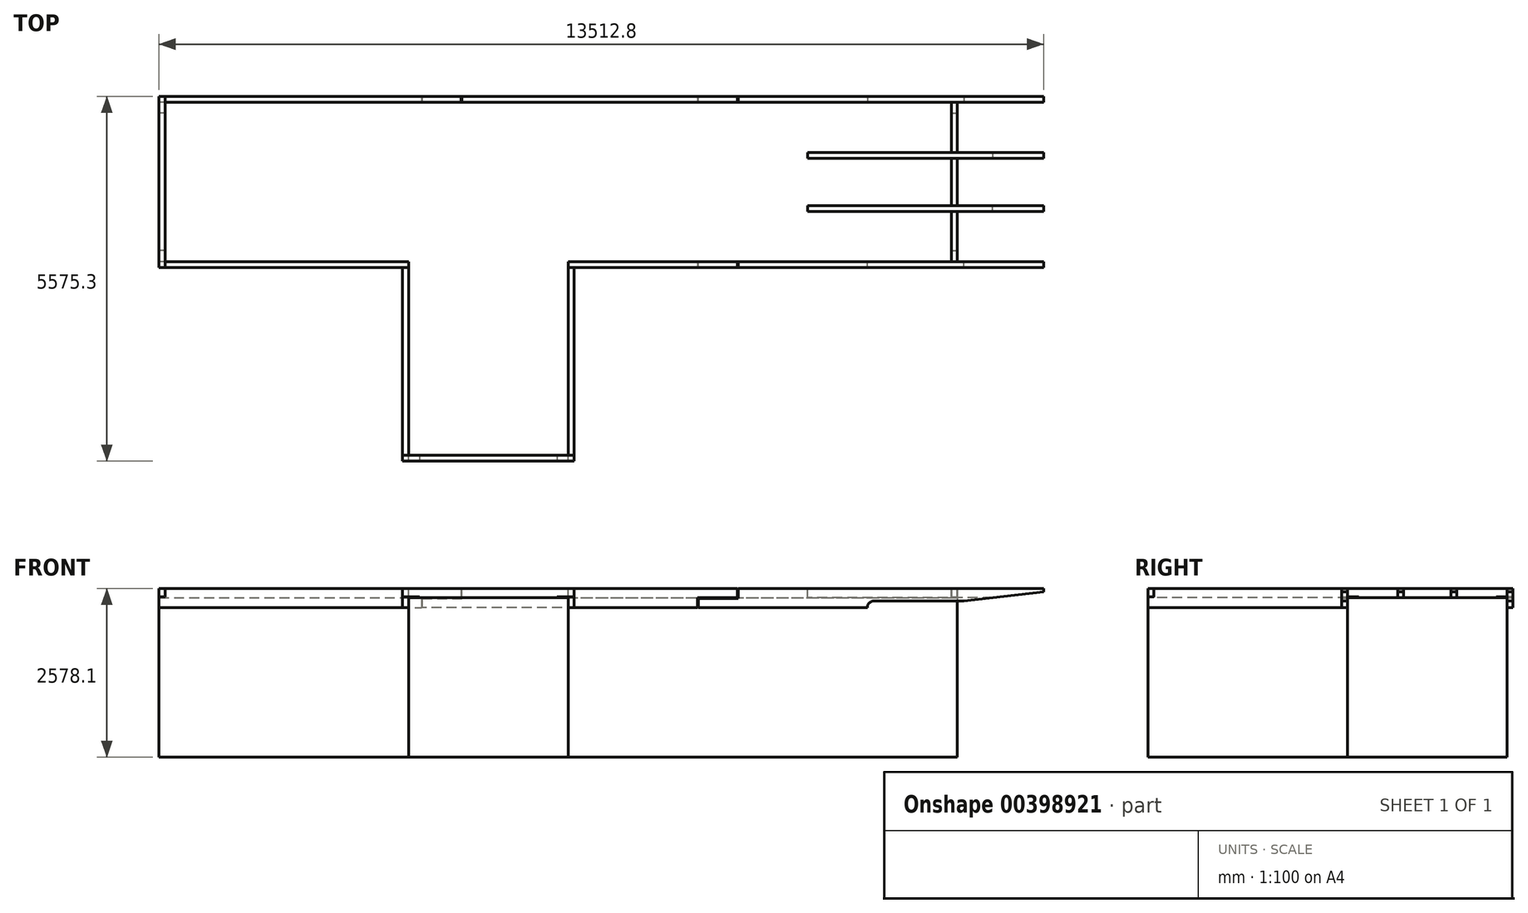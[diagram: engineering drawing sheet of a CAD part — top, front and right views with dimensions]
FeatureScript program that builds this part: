
annotation { "Feature Type Name" : "Feature", "Feature Type Description" : "" }
export const myFeature = defineFeature(function(context is Context, id is Id, definition is map)
    precondition{}
    {
        {
            var Q0;
            Q0=qCreatedBy(makeId("Top.planeOp"),FACE);
            var sketch = newSketch(context, id + "F0", { "sketchPlane" : qUnion([Q0])});
            skLineSegment(sketch, "E0.bottom", {"start": v(-6096, 1219.2) * mm, "end": v(6096, 1219.2) * mm});
            skLineSegment(sketch, "E0.top", {"start": v(-6096, -1219.2) * mm, "end": v(6096, -1219.2) * mm});
            skLineSegment(sketch, "E0.left", {"start": v(-6096, 1219.2) * mm, "end": v(-6096, -1219.2) * mm});
            skLineSegment(sketch, "E0.right", {"start": v(6096, 1219.2) * mm, "end": v(6096, -1219.2) * mm});
            skPoint(sketch, "E0.middle", {"position": v(0, 0) * mm});
            skLineSegment(sketch, "E1", {"start": v(-2286, -1219.2) * mm, "end": v(-2286, -4267.2) * mm});
            skLineSegment(sketch, "E2", {"start": v(-2286, -4267.2) * mm, "end": v(152.4, -4267.2) * mm});
            skLineSegment(sketch, "E3", {"start": v(152.4, -4267.2) * mm, "end": v(152.4, -1219.2) * mm});
            skSolve(sketch);
        }
        {
            var Q0;
            Q0=makeQuery(id+"F0.imprint","IMPRINT",FACE,{"disambiguationData":[TD([[makeQuery(id+"F0.imprint","IMPRINT",EDGE,{"derivedFrom":sQuery(id+"F0.wireOp",EDGE,"E0.bottom")}),-1.0]])]});
            var Q1;
            {var subQ0=sQuery(id+"F0.wireOp",EDGE,"E1");Q1=makeQuery(id+"F0.imprint","IMPRINT",FACE,{"disambiguationData":[TD([[makeQuery(id+"F0.imprint","IMPRINT",EDGE,{"derivedFrom":subQ0}),1.0]])]});}
            extrude(context, id + "F1", {"entities" : qUnion([Q0, Q1]), "depth" : 2438.4 * mm});
        }
        {
            var Q0;
            Q0=makeQuery(id+"F1.opExtrude","SWEPT_FACE",FACE,{"disambiguationData":[OSD([sQuery(id+"F0.wireOp",EDGE,"E0.bottom")])]});
            var sketch = newSketch(context, id + "F2", { "sketchPlane" : qUnion([Q0])});
            skLineSegment(sketch, "E4", {"start": v(-7416.8, 2578.1) * mm, "end": v(-2743.2, 2578.1) * mm});
            skLineSegment(sketch, "E5", {"start": v(-2743.2, 2578.1) * mm, "end": v(1473.2, 2578.1) * mm});
            skLineSegment(sketch, "E6", {"start": v(1473.2, 2578.1) * mm, "end": v(6096, 2578.1) * mm});
            skLineSegment(sketch, "E7", {"start": v(-7416.8, 2578.1) * mm, "end": v(-7416.8, 2527.3) * mm});
            skLineSegment(sketch, "E8", {"start": v(6096, 2578.1) * mm, "end": v(6096, 2286) * mm});
            skLineSegment(sketch, "E9", {"start": v(6096, 2286) * mm, "end": v(2082.8, 2286) * mm});
            skLineSegment(sketch, "E10", {"start": v(2082.8, 2286) * mm, "end": v(2082.8, 2432.05) * mm});
            skLineSegment(sketch, "E11", {"start": v(2082.8, 2432.05) * mm, "end": v(1473.2, 2432.05) * mm});
            skLineSegment(sketch, "E12", {"start": v(1473.2, 2578.1) * mm, "end": v(1473.2, 2432.05) * mm});
            skLineSegment(sketch, "E13", {"start": v(-2743.2, 2578.1) * mm, "end": v(-2743.2, 2432.05) * mm});
            skLineSegment(sketch, "E14", {"start": v(-2743.2, 2432.05) * mm, "end": v(-2133.6, 2432.05) * mm});
            skLineSegment(sketch, "E15", {"start": v(-2133.6, 2432.05) * mm, "end": v(-2133.6, 2286) * mm});
            skLineSegment(sketch, "E16", {"start": v(-2133.6, 2286) * mm, "end": v(2082.8, 2286) * mm});
            skLineSegment(sketch, "E17", {"start": v(-2133.6, 2286) * mm, "end": v(-4724.4, 2286) * mm});
            skLineSegment(sketch, "E18", {"start": v(-7416.8, 2527.3) * mm, "end": v(-6197.6, 2387.6) * mm});
            skLineSegment(sketch, "E19", {"start": v(-6197.6, 2387.6) * mm, "end": v(-4826, 2387.6) * mm});
            skArc(sketch, "E20", {"start": v(-4724.4, 2286) * mm, "mid": v(-4754.16, 2357.84) * mm, "end": v(-4826, 2387.6) * mm});
            skLineSegment(sketch, "E21", {"start": v(6007.1, 2578.1) * mm, "end": v(6007.1, 2454.28) * mm});
            skLineSegment(sketch, "E22", {"start": v(6007.1, 2454.28) * mm, "end": v(6096, 2454.28) * mm});
            skLineSegment(sketch, "E23", {"start": v(-152.4, 2578.1) * mm, "end": v(-152.4, 2286) * mm});
            skPoint(sketch, "E24", {"position": v(-25.4, 2286) * mm});
            skLineSegment(sketch, "E25", {"start": v(-6640.95, 2438.4) * mm, "end": v(-3810, 2438.4) * mm});
            skLineSegment(sketch, "E26", {"start": v(-3810, 2438.4) * mm, "end": v(-3810, 2578.1) * mm});
            skSolve(sketch);
        }
        {
            var Q0;
            {var subQ1=sQuery(id+"F2.wireOp",EDGE,"E4");Q0=makeQuery(id+"F2.imprint","IMPRINT",FACE,{"disambiguationData":[TD([[makeQuery(id+"F2.imprint","IMPRINT",EDGE,{"derivedFrom":subQ1}),-1.0]])]});}
            var Q1;
            {var subQ0=sQuery(id+"F2.wireOp",EDGE,"E14");Q1=makeQuery(id+"F2.imprint","IMPRINT",FACE,{"disambiguationData":[TD([[makeQuery(id+"F2.imprint","IMPRINT",EDGE,{"derivedFrom":subQ0}),-1.0]])]});}
            var Q2;
            {var subQ1=sQuery(id+"F2.wireOp",EDGE,"E7");Q2=makeQuery(id+"F2.imprint","IMPRINT",FACE,{"disambiguationData":[TD([[makeQuery(id+"F2.imprint","IMPRINT",EDGE,{"derivedFrom":subQ1}),1.0]])]});}
            var Q3;
            {var subQ0=sQuery(id+"F2.wireOp",EDGE,"E19");var subQ1=sQuery(id+"F2.wireOp",EDGE,"E18");var subQ2=makeQuery(id+"F2.imprint","INTERSECT",VERTEX,{"derivedFrom":[subQ1,subQ0]});Q3=makeQuery(id+"F2.imprint","IMPRINT",FACE,{"disambiguationData":[TD([[makeQuery(id+"F2.imprint","IMPRINT",EDGE,{"disambiguationData":[TD([[subQ2,1.0]])],"derivedFrom":subQ1}),1.0]])]});}
            extrude(context, id + "F3", {"entities" : qUnion([Q0, Q1, Q2, Q3]), "depth" : 88.9 * mm});
        }
        {
            var Q0;
            {var subQ0=sQuery(id+"F2.wireOp",EDGE,"E5");Q0=makeQuery(id+"F2.imprint","IMPRINT",FACE,{"disambiguationData":[TD([[makeQuery(id+"F2.imprint","IMPRINT",EDGE,{"derivedFrom":subQ0}),-1.0]])]});}
            var Q1;
            Q1=makeQuery(id+"F2.imprint","IMPRINT",FACE,{"disambiguationData":[TD([[makeQuery(id+"F2.imprint","IMPRINT",EDGE,{"derivedFrom":sQuery(id+"F2.wireOp",EDGE,"E10")}),1.0]])]});
            var Q2;
            {var subQ6=sQuery(id+"F2.wireOp",EDGE,"E14");Q2=makeQuery(id+"F2.imprint","IMPRINT",FACE,{"disambiguationData":[TD([[makeQuery(id+"F2.imprint","IMPRINT",EDGE,{"derivedFrom":subQ6}),1.0]])]});}
            extrude(context, id + "F4", {"entities" : qUnion([Q0, Q1, Q2]), "depth" : 88.9 * mm});
        }
        {
            var Q0;
            {var subQ0=sQuery(id+"F2.wireOp",EDGE,"E21");Q0=makeQuery(id+"F2.imprint","IMPRINT",FACE,{"disambiguationData":[TD([[makeQuery(id+"F2.imprint","IMPRINT",EDGE,{"derivedFrom":subQ0}),-1.0]])]});}
            var Q1;
            {var subQ1=sQuery(id+"F2.wireOp",EDGE,"E9");Q1=makeQuery(id+"F2.imprint","IMPRINT",FACE,{"disambiguationData":[TD([[makeQuery(id+"F2.imprint","IMPRINT",EDGE,{"derivedFrom":subQ1}),-1.0]])]});}
            extrude(context, id + "F5", {"entities" : qUnion([Q0, Q1]), "depth" : 88.9 * mm});
        }
        {
            var Q0;
            {var subQ0=sQuery(id+"F0.wireOp",EDGE,"E0.top");Q0=makeQuery(id+"F1.opExtrude","SWEPT_FACE",FACE,{"disambiguationData":[OSD([subQ0]),TDD([makeQuery(id+"F0.imprint","IMPRINT",EDGE,{"disambiguationData":[TD([[makeQuery(id+"F0.imprint","INTERSECT",VERTEX,{"derivedFrom":[subQ0,sQuery(id+"F0.wireOp",EDGE,"E0.right")]}),1.0]])],"derivedFrom":subQ0})])]});}
            var sketch = newSketch(context, id + "F6", { "sketchPlane" : qUnion([Q0])});
            skLineSegment(sketch, "E27.0", {"start": v(2743.2, 2578.1) * mm, "end": v(152.4, 2578.1) * mm});
            skLineSegment(sketch, "E27.1", {"start": v(2743.2, 2578.1) * mm, "end": v(2743.2, 2432.05) * mm});
            skLineSegment(sketch, "E27.2", {"start": v(2743.2, 2432.05) * mm, "end": v(2133.6, 2432.05) * mm});
            skLineSegment(sketch, "E27.3", {"start": v(2133.6, 2432.05) * mm, "end": v(2133.6, 2286) * mm});
            skLineSegment(sketch, "E27.4", {"start": v(2133.6, 2286) * mm, "end": v(152.4, 2286) * mm});
            skLineSegment(sketch, "E27.5", {"start": v(152.4, 2578.1) * mm, "end": v(152.4, 2286) * mm});
            skPoint(sketch, "E28.orphan", {"position": v(-1473.2, 2578.1) * mm});
            skPoint(sketch, "E29.orphan", {"position": v(-2082.8, 2286) * mm});
            skLineSegment(sketch, "E30.0", {"start": v(-2286, 2578.1) * mm, "end": v(-6096, 2578.1) * mm});
            skLineSegment(sketch, "E30.1", {"start": v(-6096, 2578.1) * mm, "end": v(-6096, 2286) * mm});
            skLineSegment(sketch, "E30.2", {"start": v(-6007.1, 2454.28) * mm, "end": v(-6096, 2454.28) * mm});
            skLineSegment(sketch, "E30.3", {"start": v(-6007.1, 2578.1) * mm, "end": v(-6007.1, 2454.28) * mm});
            skLineSegment(sketch, "E30.4", {"start": v(-6096, 2286) * mm, "end": v(-2286, 2286) * mm});
            skLineSegment(sketch, "E31", {"start": v(-2286, 2578.1) * mm, "end": v(-2286, 2286) * mm});
            skSolve(sketch);
        }
        {
            var Q0;
            {var subQ0=sQuery(id+"F6.wireOp",EDGE,"E27.0");Q0=makeQuery(id+"F6.imprint","IMPRINT",FACE,{"disambiguationData":[TD([[makeQuery(id+"F6.imprint","IMPRINT",EDGE,{"derivedFrom":subQ0}),1.0]])]});}
            var Q1;
            {var subQ1=sQuery(id+"F6.wireOp",EDGE,"E27.2");Q1=makeQuery(id+"F6.imprint","IMPRINT",FACE,{"disambiguationData":[TD([[makeQuery(id+"F6.imprint","IMPRINT",EDGE,{"derivedFrom":subQ1}),-1.0]])]});}
            extrude(context, id + "F7", {"entities" : qUnion([Q0, Q1]), "depth" : 88.9 * mm});
        }
        {
            var Q0;
            {var subQ0=sQuery(id+"F6.wireOp",EDGE,"E30.2");Q0=makeQuery(id+"F6.imprint","IMPRINT",FACE,{"disambiguationData":[TD([[makeQuery(id+"F6.imprint","IMPRINT",EDGE,{"derivedFrom":subQ0}),1.0]])]});}
            extrude(context, id + "F8", {"entities" : qUnion([Q0]), "depth" : 88.9 * mm});
        }
        {
            var Q0;
            {var subQ1=sQuery(id+"F2.wireOp",EDGE,"E9");Q0=makeQuery(id+"F2.imprint","IMPRINT",FACE,{"disambiguationData":[TD([[makeQuery(id+"F2.imprint","IMPRINT",EDGE,{"derivedFrom":subQ1}),1.0]])]});}
            cPlane(context, id + "F9", {"entities" : qUnion([Q0]), "cplaneType" : CPlaneType.OFFSET, "offset" : 812.8 * mm, "oppositeDirection" : true, "width" : 152.4 * mm, "height" : 152.4 * mm});
        }
        {
            var Q0;
            Q0=qCreatedBy(id+"F9.planeOp",FACE);
            var sketch = newSketch(context, id + "F10", { "sketchPlane" : qUnion([Q0])});
            skLineSegment(sketch, "E32.0", {"start": v(-7416.8, 2578.1) * mm, "end": v(-3810, 2578.1) * mm});
            skLineSegment(sketch, "E32.1", {"start": v(-7416.8, 2578.1) * mm, "end": v(-7416.8, 2527.3) * mm});
            skLineSegment(sketch, "E32.2", {"start": v(-7416.8, 2527.3) * mm, "end": v(-6640.95, 2438.4) * mm});
            skLineSegment(sketch, "E32.3", {"start": v(-6640.95, 2438.4) * mm, "end": v(-3810, 2438.4) * mm});
            skLineSegment(sketch, "E32.4", {"start": v(-3810, 2438.4) * mm, "end": v(-3810, 2578.1) * mm});
            skPoint(sketch, "E33.orphan", {"position": v(-6197.6, 2387.6) * mm});
            skPoint(sketch, "E34.orphan", {"position": v(-2743.2, 2578.1) * mm});
            skSolve(sketch);
        }
        {
            var Q0;
            Q0=makeQuery(id+"F10.imprint","IMPRINT",FACE,{"disambiguationData":[TD([[makeQuery(id+"F10.imprint","IMPRINT",EDGE,{"derivedFrom":sQuery(id+"F10.wireOp",EDGE,"E32.0")}),-1.0]])]});
            extrude(context, id + "F11", {"entities" : qUnion([Q0]), "endBound" : BoundingType.SYMMETRIC, "depth" : 88.9 * mm});
        }
        {
            var Q0;
            Q0=makeQuery(id+"F1.opExtrude","SWEPT_FACE",FACE,{"disambiguationData":[OSD([sQuery(id+"F0.wireOp",EDGE,"E0.left")])]});
            var sketch = newSketch(context, id + "F12", { "sketchPlane" : qUnion([Q0])});
            skLineSegment(sketch, "E35", {"start": v(-1308.1, 2578.1) * mm, "end": v(1308.1, 2578.1) * mm});
            skLineSegment(sketch, "E36", {"start": v(-1308.1, 2578.1) * mm, "end": v(-1308.1, 2454.28) * mm});
            skLineSegment(sketch, "E37", {"start": v(-1050.93, 2454.28) * mm, "end": v(-1050.93, 2438.4) * mm});
            skLineSegment(sketch, "E38", {"start": v(-1050.93, 2438.4) * mm, "end": v(1050.93, 2438.4) * mm});
            skLineSegment(sketch, "E39", {"start": v(1050.93, 2438.4) * mm, "end": v(1050.93, 2454.28) * mm});
            skLineSegment(sketch, "E40", {"start": v(1050.93, 2454.28) * mm, "end": v(1308.1, 2454.28) * mm});
            skLineSegment(sketch, "E41", {"start": v(1308.1, 2454.28) * mm, "end": v(1308.1, 2578.1) * mm});
            skLineSegment(sketch, "E42", {"start": v(-1308.1, 2454.28) * mm, "end": v(-1050.93, 2454.28) * mm});
            skSolve(sketch);
        }
        {
            var Q0;
            Q0 = qSketchRegion(id + "F12", true);
            extrude(context, id + "F13", {"entities" : qUnion([Q0]), "oppositeDirection" : true, "depth" : 88.9 * mm});
        }
        {
            var Q0;
            Q0=makeQuery(id+"F1.opExtrude","SWEPT_FACE",FACE,{"disambiguationData":[OSD([sQuery(id+"F0.wireOp",EDGE,"E1")])]});
            var sketch = newSketch(context, id + "F14", { "sketchPlane" : qUnion([Q0])});
            skLineSegment(sketch, "E43", {"start": v(1308.1, 2578.1) * mm, "end": v(4178.3, 2578.1) * mm});
            skLineSegment(sketch, "E44", {"start": v(1308.1, 2578.1) * mm, "end": v(1308.1, 2286) * mm});
            skLineSegment(sketch, "E45", {"start": v(1308.1, 2286) * mm, "end": v(4267.2, 2286) * mm});
            skLineSegment(sketch, "E46", {"start": v(4267.2, 2286) * mm, "end": v(4267.2, 2454.28) * mm});
            skLineSegment(sketch, "E47", {"start": v(4267.2, 2454.28) * mm, "end": v(4178.3, 2454.28) * mm});
            skLineSegment(sketch, "E48", {"start": v(4178.3, 2454.28) * mm, "end": v(4178.3, 2578.1) * mm});
            skSolve(sketch);
        }
        {
            var Q0;
            {var subQ2=sQuery(id+"F14.wireOp",EDGE,"E43");Q0=makeQuery(id+"F14.imprint","IMPRINT",FACE,{"disambiguationData":[TD([[makeQuery(id+"F14.imprint","IMPRINT",EDGE,{"derivedFrom":subQ2}),-1.0]])]});}
            var Q1;
            {var subQ0=sQuery(id+"F14.wireOp",EDGE,"E45");Q1=makeQuery(id+"F14.imprint","IMPRINT",FACE,{"disambiguationData":[TD([[makeQuery(id+"F14.imprint","IMPRINT",EDGE,{"derivedFrom":subQ0}),1.0]])]});}
            extrude(context, id + "F15", {"entities" : qUnion([Q0, Q1]), "depth" : 88.9 * mm});
        }
        {
            var Q0;
            Q0=makeQuery(id+"F1.opExtrude","SWEPT_FACE",FACE,{"disambiguationData":[OSD([sQuery(id+"F0.wireOp",EDGE,"E1")])]});
            var Q1;
            Q1=makeQuery(id+"F1.opExtrude","SWEPT_FACE",FACE,{"disambiguationData":[OSD([sQuery(id+"F0.wireOp",EDGE,"E3")])]});
            cPlane(context, id + "F16", {"entities" : qUnion([Q0, Q1]), "cplaneType" : CPlaneType.MID_PLANE, "offset" : 25.4 * mm, "width" : 152.4 * mm, "height" : 152.4 * mm});
        }
        {
            var Q0;
            Q0=makeQuery(id+"F15.opExtrude","SWEPT_BODY",BODY,{"disambiguationData":[OSD([sQuery(id+"F14.wireOp",EDGE,"E43"),sQuery(id+"F14.wireOp",EDGE,"E44"),sQuery(id+"F14.wireOp",EDGE,"E45"),sQuery(id+"F14.wireOp",EDGE,"E46"),sQuery(id+"F14.wireOp",EDGE,"E47"),sQuery(id+"F14.wireOp",EDGE,"E48")])]});
            var Q1;
            Q1=qCreatedBy(id+"F16.planeOp",FACE);
            mirror(context, id + "F17", {"entities" : qUnion([Q0]), "mirrorPlane" : qUnion([Q1])});
        }
        {
            var Q0;
            Q0=makeQuery(id+"F1.opExtrude","SWEPT_FACE",FACE,{"disambiguationData":[OSD([sQuery(id+"F0.wireOp",EDGE,"E2")])]});
            var sketch = newSketch(context, id + "F18", { "sketchPlane" : qUnion([Q0])});
            skLineSegment(sketch, "E49", {"start": v(-2374.9, 2578.1) * mm, "end": v(241.3, 2578.1) * mm});
            skLineSegment(sketch, "E50", {"start": v(241.3, 2578.1) * mm, "end": v(241.3, 2454.28) * mm});
            skLineSegment(sketch, "E51", {"start": v(241.3, 2454.28) * mm, "end": v(-15.87, 2454.28) * mm});
            skLineSegment(sketch, "E52", {"start": v(-15.87, 2454.28) * mm, "end": v(-15.87, 2438.4) * mm});
            skLineSegment(sketch, "E53", {"start": v(-15.87, 2438.4) * mm, "end": v(-2117.72, 2438.4) * mm});
            skLineSegment(sketch, "E54", {"start": v(-2117.72, 2438.4) * mm, "end": v(-2117.72, 2454.28) * mm});
            skLineSegment(sketch, "E55", {"start": v(-2374.9, 2578.1) * mm, "end": v(-2374.9, 2454.28) * mm});
            skLineSegment(sketch, "E56", {"start": v(-2374.9, 2454.28) * mm, "end": v(-2117.72, 2454.28) * mm});
            skSolve(sketch);
        }
        {
            var Q0;
            Q0=makeQuery(id+"F18.imprint","IMPRINT",FACE,{"disambiguationData":[TD([[makeQuery(id+"F18.imprint","IMPRINT",EDGE,{"derivedFrom":sQuery(id+"F18.wireOp",EDGE,"E49")}),-1.0]])]});
            extrude(context, id + "F19", {"entities" : qUnion([Q0]), "oppositeDirection" : true, "depth" : 88.9 * mm});
        }
        {
            var Q0;
            {var subQ0=sQuery(id+"F0.wireOp",EDGE,"E0.top");Q0=makeQuery(id+"F1.opExtrude","SWEPT_FACE",FACE,{"disambiguationData":[OSD([subQ0]),TDD([makeQuery(id+"F0.imprint","IMPRINT",EDGE,{"disambiguationData":[TD([[makeQuery(id+"F0.imprint","INTERSECT",VERTEX,{"derivedFrom":[subQ0,sQuery(id+"F0.wireOp",EDGE,"E0.left")]}),-1.0]])],"derivedFrom":subQ0})])]});}
            var Q1;
            {var subQ1=sQuery(id+"F2.wireOp",EDGE,"E9");Q1=makeQuery(id+"F2.imprint","IMPRINT",FACE,{"disambiguationData":[TD([[makeQuery(id+"F2.imprint","IMPRINT",EDGE,{"derivedFrom":subQ1}),1.0]])]});}
            cPlane(context, id + "F20", {"entities" : qUnion([Q0, Q1]), "cplaneType" : CPlaneType.MID_PLANE, "offset" : 25.4 * mm, "width" : 152.4 * mm, "height" : 152.4 * mm});
        }
        {
            var Q0;
            Q0=makeQuery(id+"F1.opExtrude","SWEPT_FACE",FACE,{"disambiguationData":[OSD([sQuery(id+"F0.wireOp",EDGE,"E0.right")])]});
            var sketch = newSketch(context, id + "F21", { "sketchPlane" : qUnion([Q0])});
            skLineSegment(sketch, "E57", {"start": v(1219.2, 2578.1) * mm, "end": v(450.85, 2578.1) * mm});
            skLineSegment(sketch, "E58", {"start": v(450.85, 2578.1) * mm, "end": v(450.85, 2438.4) * mm});
            skLineSegment(sketch, "E59", {"start": v(450.85, 2438.4) * mm, "end": v(1050.93, 2438.4) * mm});
            skLineSegment(sketch, "E60", {"start": v(1050.93, 2438.4) * mm, "end": v(1050.93, 2454.28) * mm});
            skLineSegment(sketch, "E61", {"start": v(1050.93, 2454.28) * mm, "end": v(1219.2, 2454.28) * mm});
            skLineSegment(sketch, "E62", {"start": v(1219.2, 2454.28) * mm, "end": v(1219.2, 2578.1) * mm});
            skSolve(sketch);
        }
        {
            var Q0;
            Q0 = qSketchRegion(id + "F21", true);
            extrude(context, id + "F22", {"entities" : qUnion([Q0]), "oppositeDirection" : true, "depth" : 88.9 * mm});
        }
        {
            var Q0;
            Q0=makeQuery(id+"F3.opExtrude","SWEPT_BODY",BODY,{"disambiguationData":[OSD([sQuery(id+"F2.wireOp",EDGE,"E4"),sQuery(id+"F2.wireOp",EDGE,"E7"),sQuery(id+"F2.wireOp",EDGE,"E13"),sQuery(id+"F2.wireOp",EDGE,"E14"),sQuery(id+"F2.wireOp",EDGE,"E15"),sQuery(id+"F2.wireOp",EDGE,"E17"),sQuery(id+"F2.wireOp",EDGE,"E18"),sQuery(id+"F2.wireOp",EDGE,"E19"),sQuery(id+"F2.wireOp",EDGE,"E20")])]});
            var Q1;
            Q1=makeQuery(id+"F22.opExtrude","SWEPT_BODY",BODY,{"disambiguationData":[OSD([sQuery(id+"F21.wireOp",EDGE,"E57"),sQuery(id+"F21.wireOp",EDGE,"E58"),sQuery(id+"F21.wireOp",EDGE,"E59"),sQuery(id+"F21.wireOp",EDGE,"E60"),sQuery(id+"F21.wireOp",EDGE,"E61"),sQuery(id+"F21.wireOp",EDGE,"E62")])]});
            var Q2;
            Q2=makeQuery(id+"F11.opExtrude","SWEPT_BODY",BODY,{"disambiguationData":[OSD([sQuery(id+"F10.wireOp",EDGE,"E32.0"),sQuery(id+"F10.wireOp",EDGE,"E32.1"),sQuery(id+"F10.wireOp",EDGE,"E32.2"),sQuery(id+"F10.wireOp",EDGE,"E32.3"),sQuery(id+"F10.wireOp",EDGE,"E32.4")])]});
            var Q3;
            Q3=qCreatedBy(id+"F20.planeOp",FACE);
            mirror(context, id + "F23", {"entities" : qUnion([Q0, Q1, Q2]), "mirrorPlane" : qUnion([Q3])});
        }
        {
            var Q0;
            Q0=makeQuery(id+"F1.opExtrude","SWEPT_FACE",FACE,{"disambiguationData":[OSD([sQuery(id+"F0.wireOp",EDGE,"E0.right")])]});
            var sketch = newSketch(context, id + "F24", { "sketchPlane" : qUnion([Q0])});
            skLineSegment(sketch, "E63", {"start": v(-361.95, 2578.1) * mm, "end": v(361.95, 2578.1) * mm});
            skLineSegment(sketch, "E64", {"start": v(361.95, 2578.1) * mm, "end": v(361.95, 2438.4) * mm});
            skLineSegment(sketch, "E65", {"start": v(361.95, 2438.4) * mm, "end": v(-361.95, 2438.4) * mm});
            skLineSegment(sketch, "E66", {"start": v(-361.95, 2438.4) * mm, "end": v(-361.95, 2578.1) * mm});
            skSolve(sketch);
        }
        {
            var Q0;
            Q0 = qSketchRegion(id + "F24", true);
            extrude(context, id + "F25", {"entities" : qUnion([Q0]), "oppositeDirection" : true, "depth" : 88.9 * mm});
        }
        {
            var Q0;
            Q0=makeQuery(id+"F3.opExtrude","SWEPT_EDGE",EDGE,{"disambiguationData":[OSD([sQuery(id+"F2.wireOp",EDGE,"E4"),sQuery(id+"F2.wireOp",EDGE,"E5"),sQuery(id+"F2.wireOp",EDGE,"E13")])]});
            var Q1;
            Q1=makeQuery(id+"F3.opExtrude","CAP_EDGE",EDGE,{"disambiguationData":[OSD([sQuery(id+"F2.wireOp",EDGE,"E13")])],"isStart":false});
            var Q2;
            Q2=makeQuery(id+"F3.opExtrude","CAP_EDGE",EDGE,{"disambiguationData":[OSD([sQuery(id+"F2.wireOp",EDGE,"E14")])],"isStart":false});
            var Q3;
            Q3=makeQuery(id+"F3.opExtrude","CAP_EDGE",EDGE,{"disambiguationData":[OSD([sQuery(id+"F2.wireOp",EDGE,"E15")])],"isStart":false});
            var Q4;
            Q4=makeQuery(id+"F3.opExtrude","SWEPT_EDGE",EDGE,{"disambiguationData":[OSD([sQuery(id+"F2.wireOp",EDGE,"E15"),sQuery(id+"F2.wireOp",EDGE,"E16"),sQuery(id+"F2.wireOp",EDGE,"E17")])]});
            var Q5;
            Q5=makeQuery(id+"F5.opExtrude","SWEPT_EDGE",EDGE,{"disambiguationData":[OSD([sQuery(id+"F2.wireOp",EDGE,"E5"),sQuery(id+"F2.wireOp",EDGE,"E6"),sQuery(id+"F2.wireOp",EDGE,"E12")])]});
            var Q6;
            Q6=makeQuery(id+"F5.opExtrude","CAP_EDGE",EDGE,{"disambiguationData":[OSD([sQuery(id+"F2.wireOp",EDGE,"E12")])],"isStart":false});
            var Q7;
            Q7=makeQuery(id+"F5.opExtrude","CAP_EDGE",EDGE,{"disambiguationData":[OSD([sQuery(id+"F2.wireOp",EDGE,"E11")])],"isStart":false});
            var Q8;
            Q8=makeQuery(id+"F5.opExtrude","CAP_EDGE",EDGE,{"disambiguationData":[OSD([sQuery(id+"F2.wireOp",EDGE,"E10")])],"isStart":false});
            var Q9;
            Q9=makeQuery(id+"F5.opExtrude","SWEPT_EDGE",EDGE,{"disambiguationData":[OSD([sQuery(id+"F2.wireOp",EDGE,"E9"),sQuery(id+"F2.wireOp",EDGE,"E10"),sQuery(id+"F2.wireOp",EDGE,"E16")])]});
            var Q10;
            Q10=makeQuery(id+"F7.opExtrude","CAP_EDGE",EDGE,{"disambiguationData":[OSD([sQuery(id+"F6.wireOp",EDGE,"E27.3")])],"isStart":false});
            var Q11;
            Q11=makeQuery(id+"F7.opExtrude","CAP_EDGE",EDGE,{"disambiguationData":[OSD([sQuery(id+"F6.wireOp",EDGE,"E27.2")])],"isStart":false});
            var Q12;
            Q12=makeQuery(id+"F7.opExtrude","CAP_EDGE",EDGE,{"disambiguationData":[OSD([sQuery(id+"F6.wireOp",EDGE,"E27.1")])],"isStart":false});
            var Q13;
            Q13=makeQuery(id+"F7.opExtrude","SWEPT_EDGE",EDGE,{"disambiguationData":[OSD([sQuery(id+"F6.wireOp",EDGE,"E27.0"),sQuery(id+"F6.wireOp",EDGE,"E27.1")])]});
            var Q14;
            Q14=makeQuery(id+"F7.opExtrude","SWEPT_EDGE",EDGE,{"disambiguationData":[OSD([sQuery(id+"F6.wireOp",EDGE,"E27.3"),sQuery(id+"F6.wireOp",EDGE,"E27.4")])]});
            chamfer(context, id + "F26", {"entities" : qUnion([Q0, Q1, Q2, Q3, Q4, Q5, Q6, Q7, Q8, Q9, Q10, Q11, Q12, Q13, Q14]), "width" : 6.35 * mm, "tangentPropagation" : true});
        }
        {
            var Q0;
            Q0=makeQuery(id+"F23.opPattern","COPY",EDGE,{"derivedFrom":makeQuery(id+"F3.opExtrude","CAP_EDGE",EDGE,{"disambiguationData":[OSD([sQuery(id+"F2.wireOp",EDGE,"E13")])],"isStart":false}),"instanceName":"1"});
            var Q1;
            Q1=makeQuery(id+"F23.opPattern","COPY",EDGE,{"derivedFrom":makeQuery(id+"F3.opExtrude","CAP_EDGE",EDGE,{"disambiguationData":[OSD([sQuery(id+"F2.wireOp",EDGE,"E14")])],"isStart":false}),"instanceName":"1"});
            var Q2;
            Q2=makeQuery(id+"F23.opPattern","COPY",EDGE,{"derivedFrom":makeQuery(id+"F3.opExtrude","SWEPT_EDGE",EDGE,{"disambiguationData":[OSD([sQuery(id+"F2.wireOp",EDGE,"E4"),sQuery(id+"F2.wireOp",EDGE,"E5"),sQuery(id+"F2.wireOp",EDGE,"E13")])]}),"instanceName":"1"});
            var Q3;
            Q3=makeQuery(id+"F23.opPattern","COPY",EDGE,{"derivedFrom":makeQuery(id+"F3.opExtrude","CAP_EDGE",EDGE,{"disambiguationData":[OSD([sQuery(id+"F2.wireOp",EDGE,"E15")])],"isStart":false}),"instanceName":"1"});
            var Q4;
            Q4=makeQuery(id+"F23.opPattern","COPY",EDGE,{"derivedFrom":makeQuery(id+"F3.opExtrude","SWEPT_EDGE",EDGE,{"disambiguationData":[OSD([sQuery(id+"F2.wireOp",EDGE,"E15"),sQuery(id+"F2.wireOp",EDGE,"E16"),sQuery(id+"F2.wireOp",EDGE,"E17")])]}),"instanceName":"1"});
            var Q5;
            Q5=makeQuery(id+"F4.opExtrude","CAP_EDGE",EDGE,{"disambiguationData":[OSD([sQuery(id+"F2.wireOp",EDGE,"E13")])],"isStart":false});
            var Q6;
            Q6=makeQuery(id+"F4.opExtrude","SWEPT_EDGE",EDGE,{"disambiguationData":[OSD([sQuery(id+"F2.wireOp",EDGE,"E4"),sQuery(id+"F2.wireOp",EDGE,"E5"),sQuery(id+"F2.wireOp",EDGE,"E13")])]});
            var Q7;
            Q7=makeQuery(id+"F4.opExtrude","CAP_EDGE",EDGE,{"disambiguationData":[OSD([sQuery(id+"F2.wireOp",EDGE,"E14")])],"isStart":false});
            var Q8;
            Q8=makeQuery(id+"F4.opExtrude","CAP_EDGE",EDGE,{"disambiguationData":[OSD([sQuery(id+"F2.wireOp",EDGE,"E15")])],"isStart":false});
            var Q9;
            Q9=makeQuery(id+"F4.opExtrude","SWEPT_EDGE",EDGE,{"disambiguationData":[OSD([sQuery(id+"F2.wireOp",EDGE,"E15"),sQuery(id+"F2.wireOp",EDGE,"E16"),sQuery(id+"F2.wireOp",EDGE,"E17")])]});
            var Q10;
            Q10=makeQuery(id+"F4.opExtrude","SWEPT_EDGE",EDGE,{"disambiguationData":[OSD([sQuery(id+"F2.wireOp",EDGE,"E5"),sQuery(id+"F2.wireOp",EDGE,"E6"),sQuery(id+"F2.wireOp",EDGE,"E12")])]});
            var Q11;
            Q11=makeQuery(id+"F4.opExtrude","CAP_EDGE",EDGE,{"disambiguationData":[OSD([sQuery(id+"F2.wireOp",EDGE,"E12")])],"isStart":false});
            var Q12;
            Q12=makeQuery(id+"F4.opExtrude","CAP_EDGE",EDGE,{"disambiguationData":[OSD([sQuery(id+"F2.wireOp",EDGE,"E11")])],"isStart":false});
            var Q13;
            Q13=makeQuery(id+"F4.opExtrude","CAP_EDGE",EDGE,{"disambiguationData":[OSD([sQuery(id+"F2.wireOp",EDGE,"E10")])],"isStart":false});
            var Q14;
            Q14=makeQuery(id+"F4.opExtrude","SWEPT_EDGE",EDGE,{"disambiguationData":[OSD([sQuery(id+"F2.wireOp",EDGE,"E9"),sQuery(id+"F2.wireOp",EDGE,"E10"),sQuery(id+"F2.wireOp",EDGE,"E16")])]});
            chamfer(context, id + "F27", {"entities" : qUnion([Q0, Q1, Q2, Q3, Q4, Q5, Q6, Q7, Q8, Q9, Q10, Q11, Q12, Q13, Q14]), "width" : 6.35 * mm, "tangentPropagation" : true});
        }
    });
